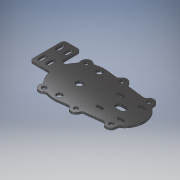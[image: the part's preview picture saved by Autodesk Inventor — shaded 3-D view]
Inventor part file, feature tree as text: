
AUTODESK INVENTOR PART (.ipt)
format: ipt  version: 2017 (Build 210142000, 142)  size: 393,728 bytes
history: native  units: mm
features: extrude x6, sketch x6, fillet x2, other x1
ambient origin geometry x8: Origin, YZ Plane, XZ Plane, XY Plane, X Axis, Y Axis, Z Axis, Center Point
bodies: Body1 (feature_tree)
feature tree (15):
  other  "Sólido1"
  extrude  "Extrusión1"  Depth=88.9mm
  extrude  "Extrusión2"  Depth=22.225mm
  fillet  "Empalme1"  Radius=22.225mm
  extrude  "Extrusión3"  Depth=22.225mm
  extrude  "Extrusión4"  TaperAngle=0.0deg  [1 undecoded]
  extrude  "Extrusión5"  Depth=4.445mm TaperAngle=0.0deg
  fillet  "Empalme2"  Radius=9.525mm
  extrude  "Extrusión6"  Depth=5.55625mm
  sketch  "Boceto1"  dims[d0=114.3mm d1=88.9mm]
  sketch  "Boceto2"  dims[d2=203.2mm d3=22.225mm d4=22.225mm]
  sketch  "Boceto3"  dims[d7=22.225mm d8=22.225mm]
  sketch  "Boceto4"  dims[d11=22.225mm d13=0.0mm]
  sketch  "Boceto5"  dims[d14=22.225mm d16=4.445mm d17=0.0mm d18=9.525mm]
  sketch  "Boceto6"  dims[d19=9.525mm d20=9.525mm d21=9.525mm d22=9.525mm d23=9.525mm d24=25.4mm d25=0.0mm d26=6.35mm d27=12.7mm d28=12.7mm d29=44.45mm d30=44.45mm d31=31.75mm d32=31.75mm d33=14.2875mm d34=12.7mm d35=12.7mm d36=45.0mm d37=45.0mm d38=25.4mm d39=0.0mm d40=12.7mm d41=56.0mm d42=56.0mm d43=28.0mm d44=28.0mm d45=0.0mm d46=93.4212mm d47=47.5mm d48=47.5mm d49=23.75mm d50=23.75mm d57=5.55625mm d58=5.159375mm d59=5.55625mm d60=5.55625mm d61=5.159375mm d62=5.159375mm d63=5.55625mm d64=5.159375mm d65=0.0mm d66=5.55625mm d67=5.55625mm d68=5.159375mm d69=5.159375mm d70=0.0mm d71=5.55625mm d72=5.55625mm d73=5.159375mm d74=5.159375mm d75=0.0mm d76=25.4mm d77=0.0mm d78=12.7mm d79=12.7mm d80=5.159375mm d81=5.159375mm d82=247.65mm d83=76.2mm d84=123.825mm d85=38.1mm d86=25.4mm d87=25.4mm d88=0.0mm d89=0.0mm d90=6.35mm d91=7.9375mm d92=18.25625mm d93=10.06475mm d94=7.9375mm d95=7.9375mm d96=5.55625mm d97=5.55625mm d98=0.0mm d99=0.0mm d100=7.9375mm d101=10.06475mm d102=18.25625mm d103=7.9375mm d104=7.9375mm d105=5.55625mm d106=5.55625mm d107=0.0mm d108=0.0mm d109=7.9375mm d110=18.25625mm d111=10.06475mm d112=7.9375mm d113=7.9375mm d114=5.55625mm d115=5.55625mm d116=0.0mm d117=0.0mm d118=7.9375mm d119=18.25625mm d120=10.06475mm d121=7.9375mm d122=7.9375mm d123=5.55625mm d124=5.55625mm d125=0.0mm d126=0.0mm d127=25.4mm d128=0.0mm]
note: 1 required parameter value undecoded (feature->parameter linkage not recoverable at this tier; creation-order binding heuristic only, values carry confidence <= 0.55)
